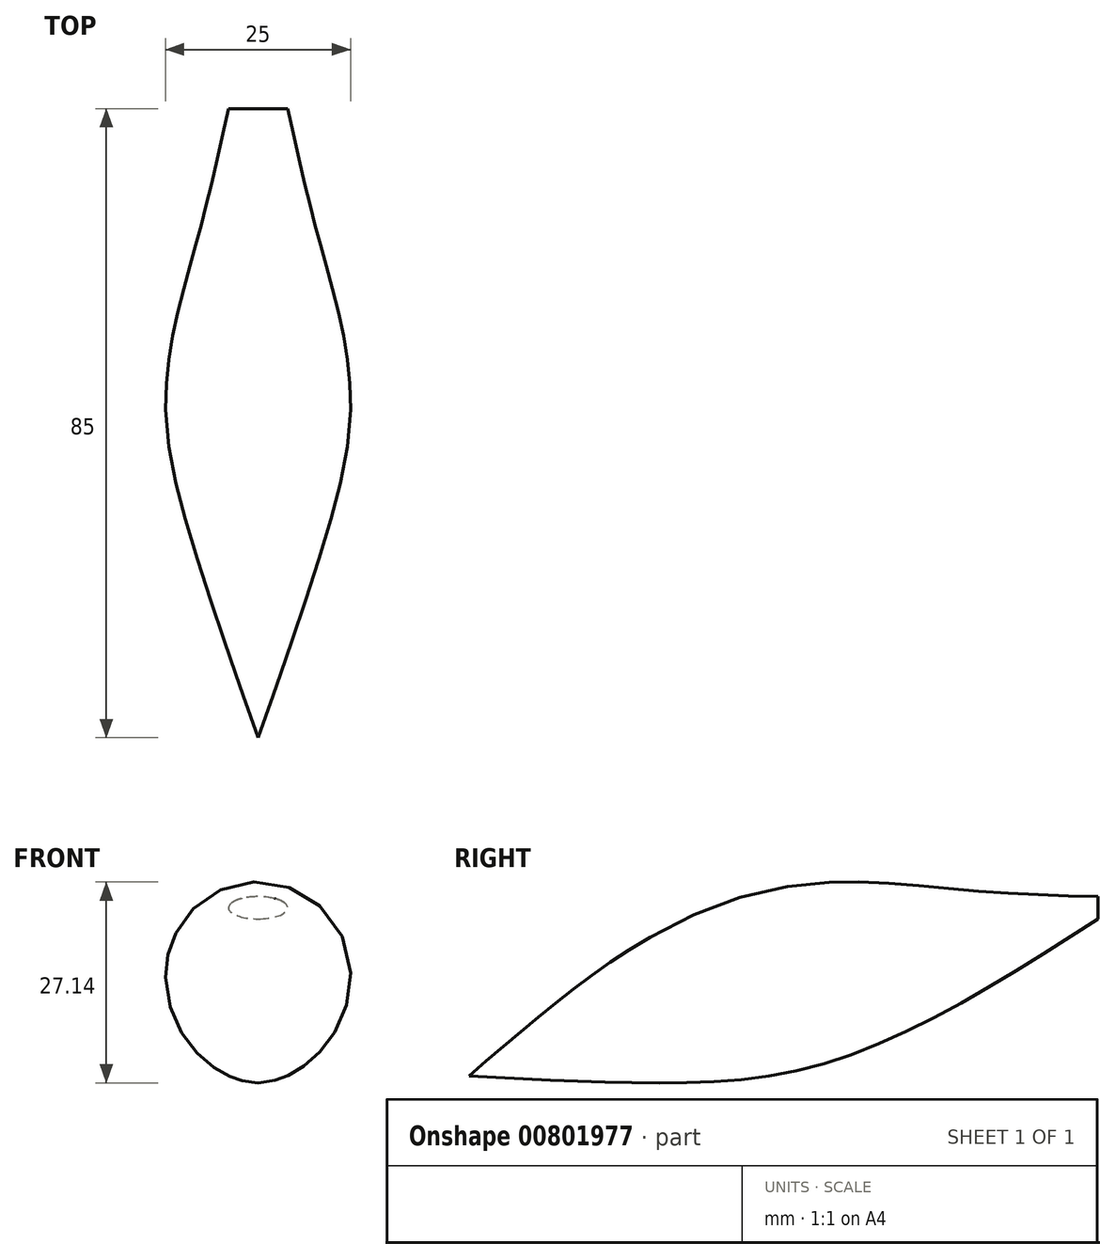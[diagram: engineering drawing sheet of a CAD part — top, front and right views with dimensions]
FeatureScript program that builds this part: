
annotation { "Feature Type Name" : "Feature", "Feature Type Description" : "" }
export const myFeature = defineFeature(function(context is Context, id is Id, definition is map)
    precondition{}
    {
        {
            var Q0;
            Q0=qCreatedBy(makeId("Front.planeOp"),FACE);
            var sketch = newSketch(context, id + "F0", { "sketchPlane" : qUnion([Q0])});
            skEllipse(sketch, "E0", {"center": v(0, 0) * mm, "majorRadius": 12.5 * mm, "minorRadius": 12.5 * mm, "majorAxis": v(1, 0)});
            skSolve(sketch);
        }
        {
            var Q0;
            Q0=qCreatedBy(makeId("Front.planeOp"),FACE);
            cPlane(context, id + "F1", {"entities" : qUnion([Q0]), "cplaneType" : CPlaneType.OFFSET, "offset" : 20 * mm, "width" : 150 * mm, "height" : 150 * mm});
        }
        {
            var Q0;
            Q0=qCreatedBy(id+"F1.planeOp",FACE);
            var sketch = newSketch(context, id + "F2", { "sketchPlane" : qUnion([Q0])});
            skEllipse(sketch, "E1", {"center": v(0, -4.3) * mm, "majorRadius": 8.5 * mm, "minorRadius": 10 * mm, "majorAxis": v(1, 0)});
            skSolve(sketch);
        }
        {
            var Q0;
            Q0=qCreatedBy(id+"F1.planeOp",FACE);
            cPlane(context, id + "F3", {"entities" : qUnion([Q0]), "cplaneType" : CPlaneType.OFFSET, "offset" : 25 * mm, "width" : 150 * mm, "height" : 150 * mm});
        }
        {
            var Q0;
            Q0=qCreatedBy(id+"F3.planeOp",FACE);
            var sketch = newSketch(context, id + "F4", { "sketchPlane" : qUnion([Q0])});
            skEllipse(sketch, "E2", {"center": v(0, -13.35) * mm, "majorRadius": 0.5 * mm, "minorRadius": 1 * mm, "majorAxis": v(1, 0)});
            skSolve(sketch);
        }
        {
            var Q0;
            Q0=qCreatedBy(makeId("Front.planeOp"),FACE);
            cPlane(context, id + "F5", {"entities" : qUnion([Q0]), "cplaneType" : CPlaneType.OFFSET, "offset" : 25 * mm, "oppositeDirection" : true, "width" : 150 * mm, "height" : 150 * mm});
        }
        {
            var Q0;
            Q0=qCreatedBy(id+"F5.planeOp",FACE);
            var sketch = newSketch(context, id + "F6", { "sketchPlane" : qUnion([Q0])});
            skEllipse(sketch, "E3", {"center": v(0, 5) * mm, "majorRadius": 7.5 * mm, "minorRadius": 6.5 * mm, "majorAxis": v(-1, 0)});
            skSolve(sketch);
        }
        {
            var Q0;
            Q0=qCreatedBy(id+"F5.planeOp",FACE);
            cPlane(context, id + "F7", {"entities" : qUnion([Q0]), "cplaneType" : CPlaneType.OFFSET, "offset" : 15 * mm, "oppositeDirection" : true, "width" : 150 * mm, "height" : 150 * mm});
        }
        {
            var Q0;
            Q0=qCreatedBy(id+"F7.planeOp",FACE);
            var sketch = newSketch(context, id + "F8", { "sketchPlane" : qUnion([Q0])});
            skEllipse(sketch, "E4", {"center": v(0, 9.36) * mm, "majorRadius": 4 * mm, "minorRadius": 1.5 * mm, "majorAxis": v(-1, 0)});
            skSolve(sketch);
        }
        {
            var Q0;
            Q0=sQuery(id+"F4.wireOp",VERTEX,"E2.center");
            var Q1;
            Q1=makeQuery(id+"F2.imprint","IMPRINT",FACE,{"disambiguationData":[TD([[makeQuery(id+"F2.imprint","IMPRINT",EDGE,{"derivedFrom":sQuery(id+"F2.wireOp",EDGE,"E1")}),1.0]])]});
            var Q2;
            Q2=makeQuery(id+"F0.imprint","IMPRINT",FACE,{"disambiguationData":[TD([[makeQuery(id+"F0.imprint","IMPRINT",EDGE,{"derivedFrom":sQuery(id+"F0.wireOp",EDGE,"E0")}),1.0]])]});
            var Q3;
            Q3=makeQuery(id+"F6.imprint","IMPRINT",FACE,{"disambiguationData":[TD([[makeQuery(id+"F6.imprint","IMPRINT",EDGE,{"derivedFrom":sQuery(id+"F6.wireOp",EDGE,"E3")}),1.0]])]});
            var Q4;
            Q4=makeQuery(id+"F8.imprint","IMPRINT",FACE,{"disambiguationData":[TD([[makeQuery(id+"F8.imprint","IMPRINT",EDGE,{"derivedFrom":sQuery(id+"F8.wireOp",EDGE,"E4")}),1.0]])]});
            loft(context, id + "F9", {"sheetProfilesArray" : [{ "sheetProfileEntities" : qUnion([Q0]) }, { "sheetProfileEntities" : qUnion([Q1]) }, { "sheetProfileEntities" : qUnion([Q2]) }, { "sheetProfileEntities" : qUnion([Q3]) }, { "sheetProfileEntities" : qUnion([Q4]) }]});
        }
    });
